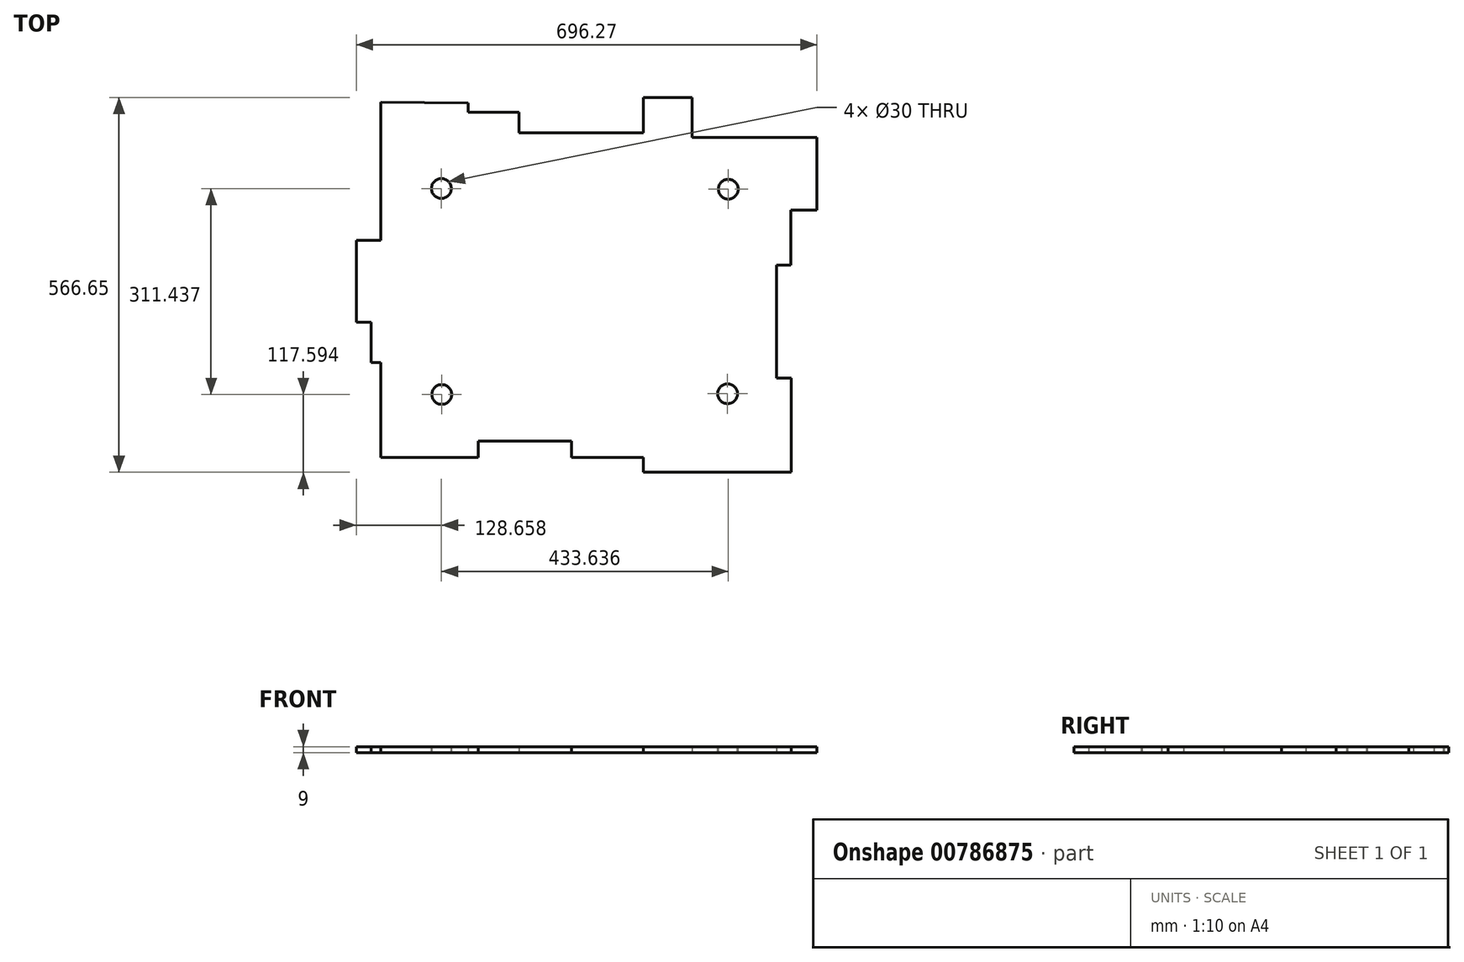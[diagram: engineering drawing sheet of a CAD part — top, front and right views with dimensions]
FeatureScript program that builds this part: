
annotation { "Feature Type Name" : "Feature", "Feature Type Description" : "" }
export const myFeature = defineFeature(function(context is Context, id is Id, definition is map)
    precondition{}
    {
        {
            var Q0;
            Q0=qCreatedBy(makeId("Top.planeOp"),FACE);
            var sketch = newSketch(context, id + "F0", { "sketchPlane" : qUnion([Q0])});
            skLineSegment(sketch, "E0", {"start": v(-215.67, 417.4) * mm, "end": v(-215.67, 208.18) * mm});
            skLineSegment(sketch, "E1", {"start": v(-215.67, 208.18) * mm, "end": v(-252.9, 208.18) * mm});
            skLineSegment(sketch, "E2", {"start": v(-252.9, 208.18) * mm, "end": v(-252.9, 84.57) * mm});
            skLineSegment(sketch, "E3", {"start": v(-252.9, 84.57) * mm, "end": v(-230.57, 84.57) * mm});
            skLineSegment(sketch, "E4", {"start": v(-230.57, 84.57) * mm, "end": v(-230.57, 23.52) * mm});
            skLineSegment(sketch, "E5", {"start": v(-230.57, 23.52) * mm, "end": v(-215.67, 23.52) * mm});
            skLineSegment(sketch, "E6", {"start": v(-215.67, 23.52) * mm, "end": v(-215.67, -120.18) * mm});
            skLineSegment(sketch, "E7", {"start": v(-215.67, -120.18) * mm, "end": v(-68.23, -120.18) * mm});
            skLineSegment(sketch, "E8", {"start": v(-68.23, -120.18) * mm, "end": v(-68.23, -95.59) * mm});
            skLineSegment(sketch, "E9", {"start": v(-68.23, -95.59) * mm, "end": v(72.52, -95.59) * mm});
            skLineSegment(sketch, "E10", {"start": v(72.52, -95.59) * mm, "end": v(72.52, -120.18) * mm});
            skLineSegment(sketch, "E11", {"start": v(72.52, -120.18) * mm, "end": v(181.24, -120.18) * mm});
            skLineSegment(sketch, "E12", {"start": v(181.24, -120.18) * mm, "end": v(181.24, -142.46) * mm});
            skLineSegment(sketch, "E13", {"start": v(181.24, -142.46) * mm, "end": v(404.64, -142.46) * mm});
            skLineSegment(sketch, "E14", {"start": v(404.64, -142.46) * mm, "end": v(404.64, 0) * mm});
            skLineSegment(sketch, "E15", {"start": v(404.64, 0) * mm, "end": v(382.3, 0) * mm});
            skLineSegment(sketch, "E16", {"start": v(382.3, 0) * mm, "end": v(382.3, 171.05) * mm});
            skLineSegment(sketch, "E17", {"start": v(382.3, 171.05) * mm, "end": v(403.9, 171.05) * mm});
            skLineSegment(sketch, "E18", {"start": v(403.9, 171.05) * mm, "end": v(403.9, 253.7) * mm});
            skLineSegment(sketch, "E19", {"start": v(403.9, 253.7) * mm, "end": v(443.36, 253.7) * mm});
            skLineSegment(sketch, "E20", {"start": v(443.36, 253.7) * mm, "end": v(443.36, 363.9) * mm});
            skLineSegment(sketch, "E21", {"start": v(443.36, 363.9) * mm, "end": v(254.96, 363.9) * mm});
            skLineSegment(sketch, "E22", {"start": v(254.96, 363.9) * mm, "end": v(254.96, 424.19) * mm});
            skLineSegment(sketch, "E23", {"start": v(254.96, 424.19) * mm, "end": v(181.24, 424.19) * mm});
            skLineSegment(sketch, "E24", {"start": v(181.24, 424.19) * mm, "end": v(181.24, 370.56) * mm});
            skLineSegment(sketch, "E25", {"start": v(181.24, 370.56) * mm, "end": v(-7.17, 370.56) * mm});
            skLineSegment(sketch, "E26", {"start": v(-7.17, 370.56) * mm, "end": v(-7.17, 401.8) * mm});
            skLineSegment(sketch, "E27", {"start": v(-7.17, 401.8) * mm, "end": v(-83.87, 401.8) * mm});
            skLineSegment(sketch, "E28", {"start": v(-83.87, 401.8) * mm, "end": v(-83.87, 415.94) * mm});
            skLineSegment(sketch, "E29", {"start": v(-83.87, 415.94) * mm, "end": v(-215.67, 417.4) * mm});
            skSolve(sketch);
        }
        {
            var Q0;
            Q0 = qSketchRegion(id + "F0", true);
            extrude(context, id + "F1", {"entities" : qUnion([Q0]), "depth" : 9 * mm, "offsetDistance" : 25 * mm});
        }
        {
            var Q0;
            Q0=makeQuery(id+"F1.opExtrude","CAP_FACE",FACE,{"disambiguationData":[OSD([sQuery(id+"F0.wireOp",EDGE,"E0"),sQuery(id+"F0.wireOp",EDGE,"E1"),sQuery(id+"F0.wireOp",EDGE,"E2"),sQuery(id+"F0.wireOp",EDGE,"E3"),sQuery(id+"F0.wireOp",EDGE,"E4"),sQuery(id+"F0.wireOp",EDGE,"E5"),sQuery(id+"F0.wireOp",EDGE,"E6"),sQuery(id+"F0.wireOp",EDGE,"E7"),sQuery(id+"F0.wireOp",EDGE,"E8"),sQuery(id+"F0.wireOp",EDGE,"E9"),sQuery(id+"F0.wireOp",EDGE,"E10"),sQuery(id+"F0.wireOp",EDGE,"E11"),sQuery(id+"F0.wireOp",EDGE,"E12"),sQuery(id+"F0.wireOp",EDGE,"E13"),sQuery(id+"F0.wireOp",EDGE,"E14"),sQuery(id+"F0.wireOp",EDGE,"E15"),sQuery(id+"F0.wireOp",EDGE,"E16"),sQuery(id+"F0.wireOp",EDGE,"E17"),sQuery(id+"F0.wireOp",EDGE,"E18"),sQuery(id+"F0.wireOp",EDGE,"E19"),sQuery(id+"F0.wireOp",EDGE,"E20"),sQuery(id+"F0.wireOp",EDGE,"E21"),sQuery(id+"F0.wireOp",EDGE,"E22"),sQuery(id+"F0.wireOp",EDGE,"E23"),sQuery(id+"F0.wireOp",EDGE,"E24"),sQuery(id+"F0.wireOp",EDGE,"E25"),sQuery(id+"F0.wireOp",EDGE,"E26"),sQuery(id+"F0.wireOp",EDGE,"E27"),sQuery(id+"F0.wireOp",EDGE,"E28"),sQuery(id+"F0.wireOp",EDGE,"E29")])],"isStart":false});
            var sketch = newSketch(context, id + "F2", { "sketchPlane" : qUnion([Q0])});
            skLineSegment(sketch, "E30.bottom", {"start": v(-124.25, 286.57) * mm, "end": v(306.67, 286.57) * mm, "construction": true});
            skLineSegment(sketch, "E30.top", {"start": v(-124.25, -23.7) * mm, "end": v(306.67, -23.7) * mm, "construction": true});
            skLineSegment(sketch, "E30.left", {"start": v(-124.25, 286.57) * mm, "end": v(-124.25, -23.7) * mm, "construction": true});
            skLineSegment(sketch, "E30.right", {"start": v(306.67, 286.57) * mm, "end": v(306.67, -23.7) * mm, "construction": true});
            skPoint(sketch, "E30.middle", {"position": v(91.2, 131.44) * mm});
            skCircle(sketch, "E31", {"center": v(-124.25, 286.57) * mm, "radius": 15 * mm});
            skCircle(sketch, "E32", {"center": v(309.38, 285.57) * mm, "radius": 15 * mm});
            skCircle(sketch, "E33", {"center": v(308.3, -23.78) * mm, "radius": 15 * mm});
            skCircle(sketch, "E34", {"center": v(-123.7, -24.87) * mm, "radius": 15 * mm});
            skSolve(sketch);
        }
        {
            var Q0;
            Q0=makeQuery(id+"F2.imprint","IMPRINT",FACE,{"disambiguationData":[TD([[makeQuery(id+"F2.imprint","IMPRINT",EDGE,{"derivedFrom":sQuery(id+"F2.wireOp",EDGE,"E31")}),1.0]])]});
            var Q1;
            Q1=makeQuery(id+"F2.imprint","IMPRINT",FACE,{"disambiguationData":[TD([[makeQuery(id+"F2.imprint","IMPRINT",EDGE,{"derivedFrom":sQuery(id+"F2.wireOp",EDGE,"E32")}),1.0]])]});
            var Q2;
            Q2=makeQuery(id+"F2.imprint","IMPRINT",FACE,{"disambiguationData":[TD([[makeQuery(id+"F2.imprint","IMPRINT",EDGE,{"derivedFrom":sQuery(id+"F2.wireOp",EDGE,"E33")}),1.0]])]});
            var Q3;
            Q3=makeQuery(id+"F2.imprint","IMPRINT",FACE,{"disambiguationData":[TD([[makeQuery(id+"F2.imprint","IMPRINT",EDGE,{"derivedFrom":sQuery(id+"F2.wireOp",EDGE,"E34")}),1.0]])]});
            var Q4;
            Q4=sQuery(id+"F2.wireOp",EDGE,"E31");
            extrude(context, id + "F3", {"entities" : qUnion([Q0, Q1, Q2, Q3]), "operationType" : NewBodyOperationType.REMOVE, "surfaceEntities" : qUnion([Q4]), "oppositeDirection" : true, "depth" : 9 * mm, "offsetDistance" : 25 * mm});
        }
    });
